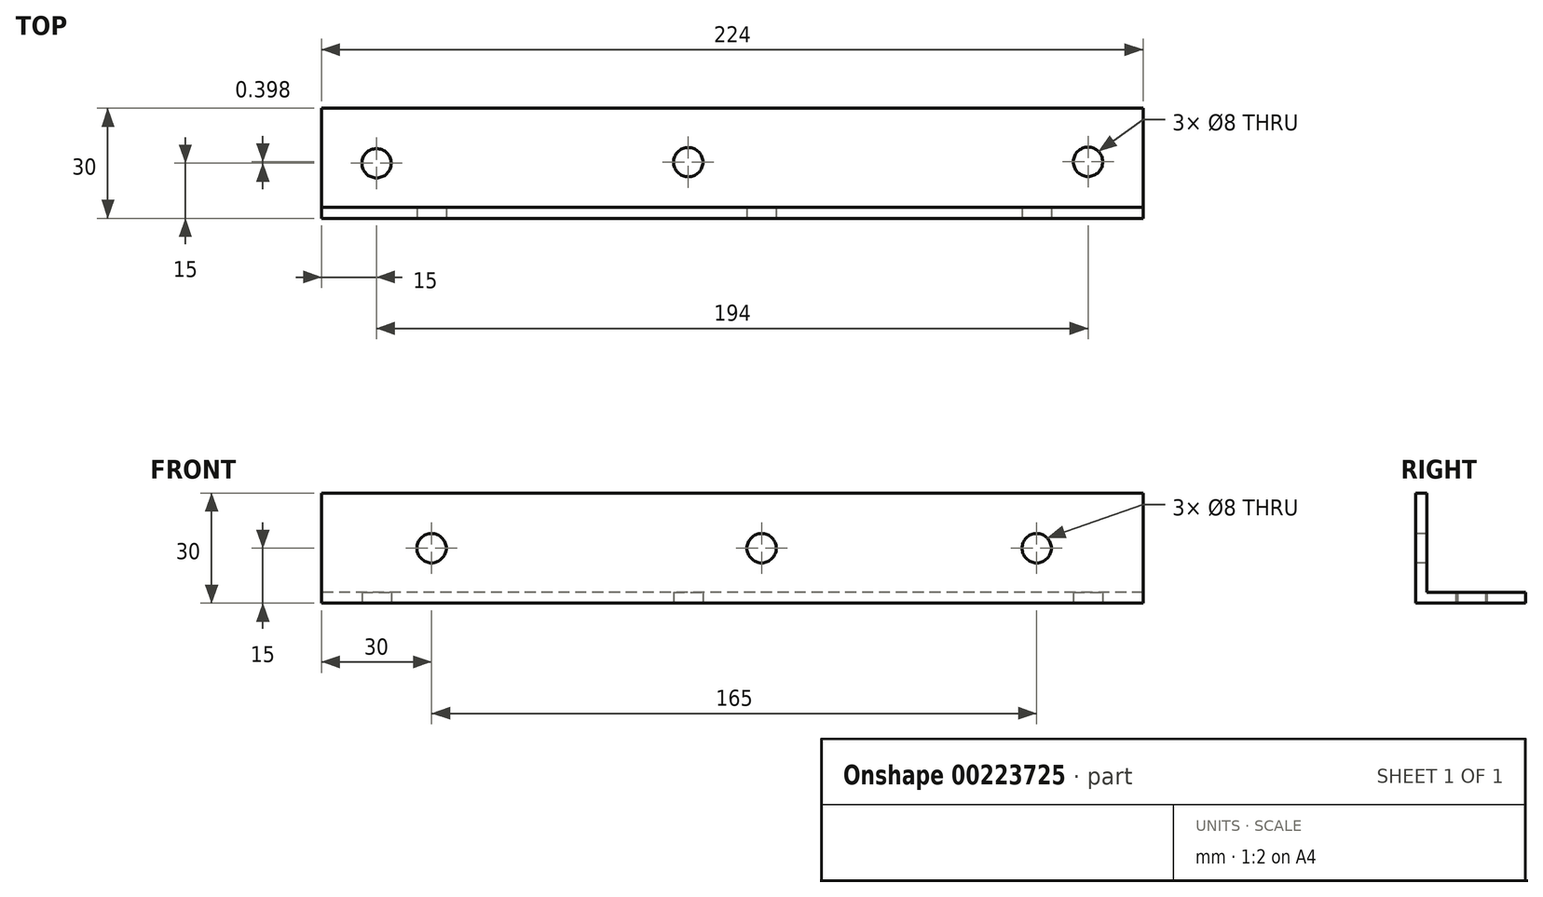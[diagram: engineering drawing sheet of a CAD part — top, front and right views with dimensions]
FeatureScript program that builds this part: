
annotation { "Feature Type Name" : "Feature", "Feature Type Description" : "" }
export const myFeature = defineFeature(function(context is Context, id is Id, definition is map)
    precondition{}
    {
        {
            var Q0;
            Q0=qCreatedBy(makeId("Right.planeOp"),FACE);
            var sketch = newSketch(context, id + "F0", { "sketchPlane" : qUnion([Q0])});
            skLineSegment(sketch, "E0", {"start": v(0, 0) * mm, "end": v(30, 0) * mm});
            skLineSegment(sketch, "E1", {"start": v(30, 0) * mm, "end": v(30, 3) * mm});
            skLineSegment(sketch, "E2", {"start": v(30, 3) * mm, "end": v(3, 3) * mm});
            skLineSegment(sketch, "E3", {"start": v(3, 3) * mm, "end": v(3, 30) * mm});
            skLineSegment(sketch, "E4", {"start": v(3, 30) * mm, "end": v(0, 30) * mm});
            skLineSegment(sketch, "E5", {"start": v(0, 30) * mm, "end": v(0, 0) * mm});
            skSolve(sketch);
        }
        {
            var Q0;
            Q0=qSketchRegion(id+"F0",true);
            extrude(context, id + "F1", {"entities" : qUnion([Q0]), "depth" : 224 * mm});
        }
        {
            var Q0;
            Q0=qCreatedBy(makeId("Top.planeOp"),FACE);
            var sketch = newSketch(context, id + "F2", { "sketchPlane" : qUnion([Q0])});
            skPoint(sketch, "E6", {"position": v(15, 15) * mm});
            skPoint(sketch, "E7", {"position": v(274.28, 15.3) * mm});
            skPoint(sketch, "E8", {"position": v(100, 15.3) * mm});
            skPoint(sketch, "E9", {"position": v(209, 15.4) * mm});
            skSolve(sketch);
        }
        {
            var Q0;
            Q0=sQuery(id+"F2.wireOp",VERTEX,"E6");
            var Q1;
            Q1=sQuery(id+"F2.wireOp",VERTEX,"E8");
            var Q2;
            Q2=sQuery(id+"F2.wireOp",VERTEX,"E9");
            var Q3;
            Q3=makeQuery(id+"F1.opExtrude","SWEPT_BODY",BODY,{"disambiguationData":[OSD([sQuery(id+"F0.wireOp",EDGE,"E0"),sQuery(id+"F0.wireOp",EDGE,"E1"),sQuery(id+"F0.wireOp",EDGE,"E2"),sQuery(id+"F0.wireOp",EDGE,"E3"),sQuery(id+"F0.wireOp",EDGE,"E4"),sQuery(id+"F0.wireOp",EDGE,"E5")])]});
            hole(context, id + "F3", {"style" : HoleStyle.SIMPLE, "endStyle" : HoleEndStyle.THROUGH, "oppositeDirection" : true, "standardTappedOrClearance" : lookupTablePath({ "standard" : "ISO", "fit" : "Close", "size" : "M5", "type" : "Clearance" }), "standardBlindInLast" : lookupTablePath({ "fit" : "Close", "standard" : "ISO", "size" : "M5", "type" : "Clearance" }), "holeDiameter" : 8 * mm, "startFromSketch" : true, "locations" : qUnion([Q0, Q1, Q2]), "scope" : qUnion([Q3]), "isTappedThrough" : true});
        }
        {
            var Q0;
            Q0=qCreatedBy(makeId("Front.planeOp"),FACE);
            var sketch = newSketch(context, id + "F4", { "sketchPlane" : qUnion([Q0])});
            skPoint(sketch, "E10", {"position": v(30, 15) * mm});
            skPoint(sketch, "E11", {"position": v(120, 15) * mm});
            skPoint(sketch, "E12", {"position": v(195, 15) * mm});
            skSolve(sketch);
        }
        {
            var Q0;
            Q0=sQuery(id+"F4.wireOp",VERTEX,"E10");
            var Q1;
            Q1=sQuery(id+"F4.wireOp",VERTEX,"E11");
            var Q2;
            Q2=sQuery(id+"F4.wireOp",VERTEX,"E12");
            var Q3;
            Q3=makeQuery(id+"F1.opExtrude","SWEPT_BODY",BODY,{"disambiguationData":[OSD([sQuery(id+"F0.wireOp",EDGE,"E0"),sQuery(id+"F0.wireOp",EDGE,"E1"),sQuery(id+"F0.wireOp",EDGE,"E2"),sQuery(id+"F0.wireOp",EDGE,"E3"),sQuery(id+"F0.wireOp",EDGE,"E4"),sQuery(id+"F0.wireOp",EDGE,"E5")])]});
            hole(context, id + "F5", {"style" : HoleStyle.SIMPLE, "endStyle" : HoleEndStyle.THROUGH, "holeDiameter" : 8 * mm, "startFromSketch" : true, "locations" : qUnion([Q0, Q1, Q2]), "scope" : qUnion([Q3]), "isTappedThrough" : true});
        }
    });
